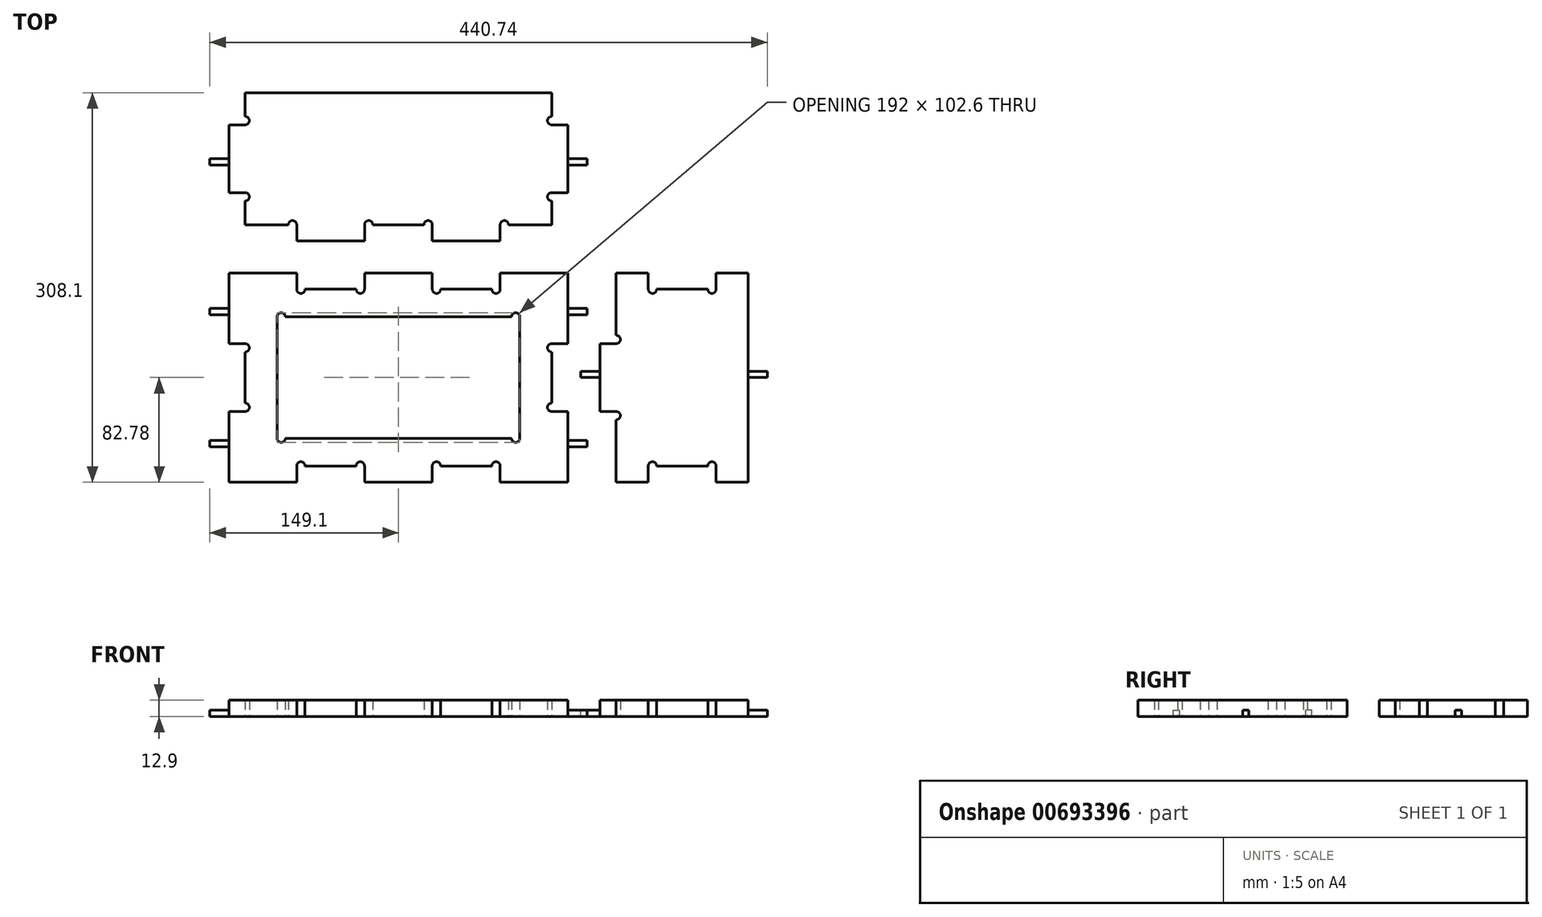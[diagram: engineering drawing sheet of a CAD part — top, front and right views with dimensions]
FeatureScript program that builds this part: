
annotation { "Feature Type Name" : "Feature", "Feature Type Description" : "" }
export const myFeature = defineFeature(function(context is Context, id is Id, definition is map)
    precondition{}
    {
        {
            assignVariable(context, id + "F0", {"name" : "thick", "anyValue" : 12.9 * mm});
        }
        {
            var Q0;
            Q0=qCreatedBy(makeId("Top.planeOp"),FACE);
            var sketch = newSketch(context, id + "F1", { "sketchPlane" : qUnion([Q0])});
            skLineSegment(sketch, "E0.bottom", {"start": v(96, -48) * mm, "end": v(-96, -48) * mm});
            skLineSegment(sketch, "E0.top", {"start": v(96, 48) * mm, "end": v(-96, 48) * mm});
            skLineSegment(sketch, "E0.left", {"start": v(96, -48) * mm, "end": v(96, 48) * mm});
            skLineSegment(sketch, "E0.right", {"start": v(-96, -48) * mm, "end": v(-96, 48) * mm});
            skPoint(sketch, "E0.middle", {"position": v(0, 0) * mm});
            skLineSegment(sketch, "E1", {"start": v(-134.1, 82.78) * mm, "end": v(-80.46, 82.78) * mm});
            skLineSegment(sketch, "E2", {"start": v(134.1, 82.78) * mm, "end": v(134.1, -82.78) * mm});
            skLineSegment(sketch, "E3", {"start": v(134.1, -82.78) * mm, "end": v(-134.1, -82.78) * mm});
            skLineSegment(sketch, "E4", {"start": v(-134.1, -82.78) * mm, "end": v(-134.1, 82.78) * mm});
            skPoint(sketch, "E5", {"position": v(0, 82.78) * mm});
            skPoint(sketch, "E6", {"position": v(134.1, 0) * mm});
            skLineSegment(sketch, "E7", {"start": v(-134.1, -82.78) * mm, "end": v(134.1, 82.78) * mm, "construction": true});
            skCircle(sketch, "E8", {"center": v(-92.7, 48) * mm, "radius": 3.3 * mm});
            skCircle(sketch, "E9", {"center": v(-92.7, -48) * mm, "radius": 3.3 * mm});
            skCircle(sketch, "E10", {"center": v(92.7, -48) * mm, "radius": 3.3 * mm});
            skCircle(sketch, "E11", {"center": v(92.7, 48) * mm, "radius": 3.3 * mm});
            skLineSegment(sketch, "E12", {"start": v(-80.46, 69.88) * mm, "end": v(-26.82, 69.88) * mm});
            skLineSegment(sketch, "E13", {"start": v(26.82, 69.88) * mm, "end": v(80.46, 69.88) * mm});
            skLineSegment(sketch, "E14", {"start": v(-80.46, 69.88) * mm, "end": v(-80.46, 82.78) * mm});
            skLineSegment(sketch, "E15", {"start": v(-26.82, 69.88) * mm, "end": v(-26.82, 82.78) * mm});
            skLineSegment(sketch, "E16", {"start": v(26.82, 69.88) * mm, "end": v(26.82, 82.78) * mm});
            skLineSegment(sketch, "E17", {"start": v(80.46, 69.88) * mm, "end": v(80.46, 82.78) * mm});
            skLineSegment(sketch, "E18", {"start": v(-80.46, 82.78) * mm, "end": v(-26.82, 82.78) * mm});
            skLineSegment(sketch, "E19", {"start": v(-26.82, 82.78) * mm, "end": v(26.82, 82.78) * mm});
            skLineSegment(sketch, "E20", {"start": v(26.82, 82.78) * mm, "end": v(80.46, 82.78) * mm});
            skLineSegment(sketch, "E21", {"start": v(80.46, 82.78) * mm, "end": v(134.1, 82.78) * mm});
            skLineSegment(sketch, "E22", {"start": v(-80.46, -82.78) * mm, "end": v(-80.46, -69.88) * mm});
            skLineSegment(sketch, "E23", {"start": v(-80.46, -69.88) * mm, "end": v(-26.82, -69.88) * mm});
            skLineSegment(sketch, "E24", {"start": v(-26.82, -69.88) * mm, "end": v(-26.82, -82.78) * mm});
            skLineSegment(sketch, "E25", {"start": v(26.82, -82.78) * mm, "end": v(26.82, -69.88) * mm});
            skLineSegment(sketch, "E26", {"start": v(26.82, -69.88) * mm, "end": v(80.46, -69.88) * mm});
            skLineSegment(sketch, "E27", {"start": v(80.46, -69.88) * mm, "end": v(80.46, -82.78) * mm});
            skLineSegment(sketch, "E28", {"start": v(134.1, 26.82) * mm, "end": v(121.2, 26.82) * mm});
            skLineSegment(sketch, "E29", {"start": v(121.2, 26.82) * mm, "end": v(121.2, -26.82) * mm});
            skLineSegment(sketch, "E30", {"start": v(121.2, -26.82) * mm, "end": v(134.1, -26.82) * mm});
            skPoint(sketch, "E31", {"position": v(121.2, 0) * mm});
            skLineSegment(sketch, "E32", {"start": v(-134.1, 26.82) * mm, "end": v(-121.2, 26.82) * mm});
            skLineSegment(sketch, "E33", {"start": v(-121.2, 26.82) * mm, "end": v(-121.2, -26.82) * mm});
            skLineSegment(sketch, "E34", {"start": v(-121.2, -26.82) * mm, "end": v(-134.1, -26.82) * mm});
            skCircle(sketch, "E35", {"center": v(-77.16, 69.88) * mm, "radius": 3.3 * mm});
            skCircle(sketch, "E36", {"center": v(-30.12, 69.88) * mm, "radius": 3.3 * mm});
            skCircle(sketch, "E37", {"center": v(30.12, 69.88) * mm, "radius": 3.3 * mm});
            skCircle(sketch, "E38", {"center": v(77.16, 69.88) * mm, "radius": 3.3 * mm});
            skCircle(sketch, "E39", {"center": v(121.2, 23.52) * mm, "radius": 3.3 * mm});
            skCircle(sketch, "E40", {"center": v(121.2, -23.52) * mm, "radius": 3.3 * mm});
            skCircle(sketch, "E41", {"center": v(77.16, -69.88) * mm, "radius": 3.3 * mm});
            skCircle(sketch, "E42", {"center": v(30.12, -69.88) * mm, "radius": 3.3 * mm});
            skCircle(sketch, "E43", {"center": v(-30.12, -69.88) * mm, "radius": 3.3 * mm});
            skCircle(sketch, "E44", {"center": v(-77.16, -69.88) * mm, "radius": 3.3 * mm});
            skCircle(sketch, "E45", {"center": v(-121.2, -23.52) * mm, "radius": 3.3 * mm});
            skCircle(sketch, "E46", {"center": v(-121.2, 23.52) * mm, "radius": 3.3 * mm});
            skLineSegment(sketch, "E47", {"start": v(-121.2, 120.88) * mm, "end": v(121.2, 120.88) * mm});
            skLineSegment(sketch, "E48", {"start": v(121.2, 120.88) * mm, "end": v(121.2, 225.32) * mm});
            skLineSegment(sketch, "E49", {"start": v(121.2, 225.32) * mm, "end": v(-121.2, 225.32) * mm});
            skLineSegment(sketch, "E50", {"start": v(-121.2, 225.32) * mm, "end": v(-121.2, 120.88) * mm});
            skLineSegment(sketch, "E51", {"start": v(-80.46, 120.88) * mm, "end": v(-80.46, 107.98) * mm});
            skLineSegment(sketch, "E52", {"start": v(-80.46, 107.98) * mm, "end": v(-26.82, 107.98) * mm});
            skLineSegment(sketch, "E53", {"start": v(-26.82, 107.98) * mm, "end": v(-26.82, 120.88) * mm});
            skLineSegment(sketch, "E54", {"start": v(26.82, 120.88) * mm, "end": v(26.82, 107.98) * mm});
            skLineSegment(sketch, "E55", {"start": v(26.82, 107.98) * mm, "end": v(80.46, 107.98) * mm});
            skLineSegment(sketch, "E56", {"start": v(80.46, 107.98) * mm, "end": v(80.46, 120.88) * mm});
            skCircle(sketch, "E57", {"center": v(23.52, 120.88) * mm, "radius": 3.3 * mm});
            skCircle(sketch, "E58", {"center": v(-23.52, 120.88) * mm, "radius": 3.3 * mm});
            skCircle(sketch, "E59", {"center": v(-83.76, 120.88) * mm, "radius": 3.3 * mm});
            skCircle(sketch, "E60", {"center": v(83.76, 120.88) * mm, "radius": 3.3 * mm});
            skLineSegment(sketch, "E61", {"start": v(134.1, 199.92) * mm, "end": v(134.1, 146.28) * mm});
            skPoint(sketch, "E62", {"position": v(121.2, 173.1) * mm});
            skPoint(sketch, "E63", {"position": v(134.1, 173.1) * mm});
            skLineSegment(sketch, "E64", {"start": v(134.1, 199.92) * mm, "end": v(121.2, 199.92) * mm});
            skLineSegment(sketch, "E65", {"start": v(134.1, 146.28) * mm, "end": v(121.2, 146.28) * mm});
            skCircle(sketch, "E66", {"center": v(121.2, 142.98) * mm, "radius": 3.3 * mm});
            skCircle(sketch, "E67", {"center": v(121.2, 203.22) * mm, "radius": 3.3 * mm});
            skLineSegment(sketch, "E68", {"start": v(-121.2, 146.28) * mm, "end": v(-134.1, 146.28) * mm});
            skLineSegment(sketch, "E69", {"start": v(-134.1, 146.28) * mm, "end": v(-134.1, 199.92) * mm});
            skLineSegment(sketch, "E70", {"start": v(-134.1, 199.92) * mm, "end": v(-121.2, 199.92) * mm});
            skCircle(sketch, "E71", {"center": v(-121.2, 203.22) * mm, "radius": 3.3 * mm});
            skCircle(sketch, "E72", {"center": v(-121.2, 142.98) * mm, "radius": 3.3 * mm});
            skLineSegment(sketch, "E73", {"start": v(172.2, 82.78) * mm, "end": v(172.2, -82.78) * mm});
            skLineSegment(sketch, "E74", {"start": v(276.64, -82.78) * mm, "end": v(276.64, 82.78) * mm});
            skLineSegment(sketch, "E75", {"start": v(276.64, 82.78) * mm, "end": v(172.2, 82.78) * mm});
            skLineSegment(sketch, "E76", {"start": v(172.2, 26.82) * mm, "end": v(159.3, 26.82) * mm});
            skLineSegment(sketch, "E77", {"start": v(159.3, 26.82) * mm, "end": v(159.3, -26.82) * mm});
            skLineSegment(sketch, "E78", {"start": v(159.3, -26.82) * mm, "end": v(172.2, -26.82) * mm});
            skLineSegment(sketch, "E79", {"start": v(172.2, -82.78) * mm, "end": v(276.64, -82.78) * mm});
            skLineSegment(sketch, "E80", {"start": v(197.6, 82.78) * mm, "end": v(197.6, 69.88) * mm});
            skLineSegment(sketch, "E81", {"start": v(197.6, 69.88) * mm, "end": v(251.24, 69.88) * mm});
            skLineSegment(sketch, "E82", {"start": v(251.24, 69.88) * mm, "end": v(251.24, 82.78) * mm});
            skLineSegment(sketch, "E83", {"start": v(197.6, -82.78) * mm, "end": v(197.6, -69.88) * mm});
            skLineSegment(sketch, "E84", {"start": v(197.6, -69.88) * mm, "end": v(251.24, -69.88) * mm});
            skLineSegment(sketch, "E85", {"start": v(251.24, -69.88) * mm, "end": v(251.24, -82.78) * mm});
            skPoint(sketch, "E86", {"position": v(224.42, 69.88) * mm});
            skPoint(sketch, "E87", {"position": v(224.42, 82.78) * mm});
            skCircle(sketch, "E88", {"center": v(172.2, 30.12) * mm, "radius": 3.3 * mm});
            skCircle(sketch, "E89", {"center": v(172.2, -30.12) * mm, "radius": 3.3 * mm});
            skCircle(sketch, "E90", {"center": v(200.9, -69.88) * mm, "radius": 3.3 * mm});
            skCircle(sketch, "E91", {"center": v(247.94, -69.88) * mm, "radius": 3.3 * mm});
            skCircle(sketch, "E92", {"center": v(247.94, 69.88) * mm, "radius": 3.3 * mm});
            skCircle(sketch, "E93", {"center": v(200.9, 69.88) * mm, "radius": 3.3 * mm});
            skLineSegment(sketch, "E94", {"start": v(-121.2, 120.88) * mm, "end": v(-121.2, 82.78) * mm, "construction": true});
            skLineSegment(sketch, "E95", {"start": v(121.2, 120.88) * mm, "end": v(121.2, 82.78) * mm, "construction": true});
            skLineSegment(sketch, "E96", {"start": v(-121.2, 101.83) * mm, "end": v(121.2, 101.83) * mm, "construction": true});
            skSolve(sketch);
        }
        {
            var Q0;
            {var subQ48=sQuery(id+"F1.wireOp",EDGE,"E0.left");Q0=makeQuery(id+"F1.imprint","IMPRINT",FACE,{"disambiguationData":[TD([[makeQuery(id+"F1.imprint","IMPRINT",EDGE,{"derivedFrom":subQ48}),-1.0]])]});}
            extrude(context, id + "F2", {"entities" : qUnion([Q0]), "depth" : getVariable(context, 'thick'), "offsetDistance" : 25 * mm});
        }
        {
            var Q0;
            {var subQ0=sQuery(id+"F1.wireOp",EDGE,"E49");Q0=makeQuery(id+"F1.imprint","IMPRINT",FACE,{"disambiguationData":[TD([[makeQuery(id+"F1.imprint","IMPRINT",EDGE,{"derivedFrom":subQ0}),1.0]])]});}
            var Q1;
            {var subQ0=sQuery(id+"F1.wireOp",EDGE,"E68");Q1=makeQuery(id+"F1.imprint","IMPRINT",FACE,{"disambiguationData":[TD([[makeQuery(id+"F1.imprint","IMPRINT",EDGE,{"derivedFrom":subQ0}),-1.0]])]});}
            var Q2;
            {var subQ0=sQuery(id+"F1.wireOp",EDGE,"E51");Q2=makeQuery(id+"F1.imprint","IMPRINT",FACE,{"disambiguationData":[TD([[makeQuery(id+"F1.imprint","IMPRINT",EDGE,{"derivedFrom":subQ0}),1.0]])]});}
            var Q3;
            {var subQ0=sQuery(id+"F1.wireOp",EDGE,"E54");Q3=makeQuery(id+"F1.imprint","IMPRINT",FACE,{"disambiguationData":[TD([[makeQuery(id+"F1.imprint","IMPRINT",EDGE,{"derivedFrom":subQ0}),1.0]])]});}
            var Q4;
            Q4=makeQuery(id+"F1.imprint","IMPRINT",FACE,{"disambiguationData":[TD([[makeQuery(id+"F1.imprint","IMPRINT",EDGE,{"derivedFrom":sQuery(id+"F1.wireOp",EDGE,"E61")}),-1.0]])]});
            extrude(context, id + "F3", {"entities" : qUnion([Q0, Q1, Q2, Q3, Q4]), "depth" : getVariable(context, 'thick'), "offsetDistance" : 25 * mm});
        }
        {
            var Q0;
            {var subQ1=sQuery(id+"F1.wireOp",EDGE,"E74");Q0=makeQuery(id+"F1.imprint","IMPRINT",FACE,{"disambiguationData":[TD([[makeQuery(id+"F1.imprint","IMPRINT",EDGE,{"derivedFrom":subQ1}),1.0]])]});}
            var Q1;
            {var subQ0=sQuery(id+"F1.wireOp",EDGE,"E76");Q1=makeQuery(id+"F1.imprint","IMPRINT",FACE,{"disambiguationData":[TD([[makeQuery(id+"F1.imprint","IMPRINT",EDGE,{"derivedFrom":subQ0}),1.0]])]});}
            extrude(context, id + "F4", {"entities" : qUnion([Q0, Q1]), "depth" : getVariable(context, 'thick'), "offsetDistance" : 25 * mm});
        }
        {
            var Q0;
            {var subQ0=sQuery(id+"F1.wireOp",EDGE,"E4");Q0=makeQuery(id+"F2.opExtrude","SWEPT_FACE",FACE,{"disambiguationData":[OSD([subQ0]),TDD([makeQuery(id+"F1.imprint","IMPRINT",EDGE,{"disambiguationData":[TD([[makeQuery(id+"F1.imprint","INTERSECT",VERTEX,{"derivedFrom":[sQuery(id+"F1.wireOp",EDGE,"E1"),subQ0]}),1.0]])],"derivedFrom":subQ0})])]});}
            var sketch = newSketch(context, id + "F5", { "sketchPlane" : qUnion([Q0])});
            skLineSegment(sketch, "E97", {"start": v(-54.8, 5) * mm, "end": v(-49.8, 5) * mm});
            skLineSegment(sketch, "E98", {"start": v(-49.8, 5) * mm, "end": v(-49.8, 0) * mm});
            skLineSegment(sketch, "E99", {"start": v(-49.8, 0) * mm, "end": v(-54.8, 0) * mm});
            skLineSegment(sketch, "E100", {"start": v(-54.8, 0) * mm, "end": v(-54.8, 5) * mm});
            skSolve(sketch);
        }
        {
            var Q0;
            Q0=makeQuery(id+"F5.imprint","IMPRINT",FACE,{"disambiguationData":[TD([[makeQuery(id+"F5.imprint","IMPRINT",EDGE,{"derivedFrom":sQuery(id+"F5.wireOp",EDGE,"E97")}),-1.0]])]});
            extrude(context, id + "F6", {"entities" : qUnion([Q0]), "operationType" : NewBodyOperationType.ADD, "depth" : 15 * mm, "offsetDistance" : 25 * mm});
        }
        {
            var Q0;
            {var subQ0=sQuery(id+"F1.wireOp",EDGE,"E4");Q0=makeQuery(id+"F2.opExtrude","SWEPT_FACE",FACE,{"disambiguationData":[OSD([subQ0]),TDD([makeQuery(id+"F1.imprint","IMPRINT",EDGE,{"disambiguationData":[TD([[makeQuery(id+"F1.imprint","INTERSECT",VERTEX,{"derivedFrom":[sQuery(id+"F1.wireOp",EDGE,"E3"),subQ0]}),-1.0]])],"derivedFrom":subQ0})])]});}
            var sketch = newSketch(context, id + "F7", { "sketchPlane" : qUnion([Q0])});
            skLineSegment(sketch, "E101.bottom", {"start": v(54.8, 0) * mm, "end": v(49.8, 0) * mm});
            skLineSegment(sketch, "E101.top", {"start": v(54.8, 5) * mm, "end": v(49.8, 5) * mm});
            skLineSegment(sketch, "E101.left", {"start": v(54.8, 0) * mm, "end": v(54.8, 5) * mm});
            skLineSegment(sketch, "E101.right", {"start": v(49.8, 0) * mm, "end": v(49.8, 5) * mm});
            skSolve(sketch);
        }
        {
            var Q0;
            Q0=makeQuery(id+"F7.imprint","IMPRINT",FACE,{"disambiguationData":[TD([[makeQuery(id+"F7.imprint","IMPRINT",EDGE,{"derivedFrom":sQuery(id+"F7.wireOp",EDGE,"E101.bottom")}),-1.0]])]});
            extrude(context, id + "F8", {"entities" : qUnion([Q0]), "operationType" : NewBodyOperationType.ADD, "depth" : 15 * mm, "offsetDistance" : 25 * mm});
        }
        {
            var Q0;
            {var subQ0=sQuery(id+"F1.wireOp",EDGE,"E2");Q0=makeQuery(id+"F2.opExtrude","SWEPT_FACE",FACE,{"disambiguationData":[OSD([subQ0]),TDD([makeQuery(id+"F1.imprint","IMPRINT",EDGE,{"disambiguationData":[TD([[makeQuery(id+"F1.imprint","INTERSECT",VERTEX,{"derivedFrom":[subQ0,sQuery(id+"F1.wireOp",EDGE,"E3")]}),1.0]])],"derivedFrom":subQ0})])]});}
            var sketch = newSketch(context, id + "F9", { "sketchPlane" : qUnion([Q0])});
            skLineSegment(sketch, "E102.bottom", {"start": v(-54.8, 0) * mm, "end": v(-49.8, 0) * mm});
            skLineSegment(sketch, "E102.top", {"start": v(-54.8, 5) * mm, "end": v(-49.8, 5) * mm});
            skLineSegment(sketch, "E102.left", {"start": v(-54.8, 0) * mm, "end": v(-54.8, 5) * mm});
            skLineSegment(sketch, "E102.right", {"start": v(-49.8, 0) * mm, "end": v(-49.8, 5) * mm});
            skSolve(sketch);
        }
        {
            var Q0;
            Q0=makeQuery(id+"F9.imprint","IMPRINT",FACE,{"disambiguationData":[TD([[makeQuery(id+"F9.imprint","IMPRINT",EDGE,{"derivedFrom":sQuery(id+"F9.wireOp",EDGE,"E102.bottom")}),-1.0]])]});
            extrude(context, id + "F10", {"entities" : qUnion([Q0]), "operationType" : NewBodyOperationType.ADD, "depth" : 15 * mm, "offsetDistance" : 25 * mm});
        }
        {
            var Q0;
            {var subQ0=sQuery(id+"F1.wireOp",EDGE,"E2");Q0=makeQuery(id+"F2.opExtrude","SWEPT_FACE",FACE,{"disambiguationData":[OSD([subQ0]),TDD([makeQuery(id+"F1.imprint","IMPRINT",EDGE,{"disambiguationData":[TD([[makeQuery(id+"F1.imprint","INTERSECT",VERTEX,{"derivedFrom":[subQ0,sQuery(id+"F1.wireOp",EDGE,"E21")]}),-1.0]])],"derivedFrom":subQ0})])]});}
            var sketch = newSketch(context, id + "F11", { "sketchPlane" : qUnion([Q0])});
            skLineSegment(sketch, "E103.bottom", {"start": v(54.8, 0) * mm, "end": v(49.8, 0) * mm});
            skLineSegment(sketch, "E103.top", {"start": v(54.8, 5) * mm, "end": v(49.8, 5) * mm});
            skLineSegment(sketch, "E103.left", {"start": v(54.8, 0) * mm, "end": v(54.8, 5) * mm});
            skLineSegment(sketch, "E103.right", {"start": v(49.8, 0) * mm, "end": v(49.8, 5) * mm});
            skSolve(sketch);
        }
        {
            var Q0;
            Q0=qSketchRegion(id+"F11",true);
            extrude(context, id + "F12", {"entities" : qUnion([Q0]), "operationType" : NewBodyOperationType.ADD, "depth" : 15 * mm, "offsetDistance" : 25 * mm});
        }
        {
            var Q0;
            Q0=makeQuery(id+"F3.opExtrude","SWEPT_FACE",FACE,{"disambiguationData":[OSD([sQuery(id+"F1.wireOp",EDGE,"E69")])]});
            var sketch = newSketch(context, id + "F13", { "sketchPlane" : qUnion([Q0])});
            skLineSegment(sketch, "E104.bottom", {"start": v(-173.1, 0) * mm, "end": v(-168.1, 0) * mm});
            skLineSegment(sketch, "E104.top", {"start": v(-173.1, 5) * mm, "end": v(-168.1, 5) * mm});
            skLineSegment(sketch, "E104.left", {"start": v(-173.1, 0) * mm, "end": v(-173.1, 5) * mm});
            skLineSegment(sketch, "E104.right", {"start": v(-168.1, 0) * mm, "end": v(-168.1, 5) * mm});
            skSolve(sketch);
        }
        {
            var Q0;
            Q0=qSketchRegion(id+"F13",true);
            var Q1;
            Q1=makeQuery(id+"F13.imprint","IMPRINT",FACE,{"disambiguationData":[TD([[makeQuery(id+"F13.imprint","IMPRINT",EDGE,{"derivedFrom":sQuery(id+"F13.wireOp",EDGE,"E104.bottom")}),-1.0]])]});
            extrude(context, id + "F14", {"entities" : qUnion([Q0, Q1]), "operationType" : NewBodyOperationType.ADD, "depth" : 15 * mm, "offsetDistance" : 25 * mm});
        }
        {
            var Q0;
            Q0=makeQuery(id+"F3.opExtrude","SWEPT_FACE",FACE,{"disambiguationData":[OSD([sQuery(id+"F1.wireOp",EDGE,"E61")])]});
            var sketch = newSketch(context, id + "F15", { "sketchPlane" : qUnion([Q0])});
            skLineSegment(sketch, "E105.bottom", {"start": v(173.1, 0) * mm, "end": v(168.1, 0) * mm});
            skLineSegment(sketch, "E105.top", {"start": v(173.1, 5) * mm, "end": v(168.1, 5) * mm});
            skLineSegment(sketch, "E105.left", {"start": v(173.1, 0) * mm, "end": v(173.1, 5) * mm});
            skLineSegment(sketch, "E105.right", {"start": v(168.1, 0) * mm, "end": v(168.1, 5) * mm});
            skSolve(sketch);
        }
        {
            var Q0;
            Q0=qSketchRegion(id+"F15",true);
            extrude(context, id + "F16", {"entities" : qUnion([Q0]), "operationType" : NewBodyOperationType.ADD, "depth" : 15 * mm, "offsetDistance" : 25 * mm});
        }
        {
            var Q0;
            Q0=makeQuery(id+"F4.opExtrude","SWEPT_FACE",FACE,{"disambiguationData":[OSD([sQuery(id+"F1.wireOp",EDGE,"E77")])]});
            var sketch = newSketch(context, id + "F17", { "sketchPlane" : qUnion([Q0])});
            skLineSegment(sketch, "E106.bottom", {"start": v(0, 0) * mm, "end": v(-5, 0) * mm});
            skLineSegment(sketch, "E106.top", {"start": v(0, 5) * mm, "end": v(-5, 5) * mm});
            skLineSegment(sketch, "E106.left", {"start": v(0, 0) * mm, "end": v(0, 5) * mm});
            skLineSegment(sketch, "E106.right", {"start": v(-5, 0) * mm, "end": v(-5, 5) * mm});
            skSolve(sketch);
        }
        {
            var Q0;
            Q0=makeQuery(id+"F17.imprint","IMPRINT",FACE,{"disambiguationData":[TD([[makeQuery(id+"F17.imprint","IMPRINT",EDGE,{"derivedFrom":sQuery(id+"F17.wireOp",EDGE,"E106.bottom")}),1.0]])]});
            extrude(context, id + "F18", {"entities" : qUnion([Q0]), "operationType" : NewBodyOperationType.ADD, "depth" : 15 * mm, "offsetDistance" : 25 * mm});
        }
        {
            var Q0;
            Q0=makeQuery(id+"F4.opExtrude","SWEPT_FACE",FACE,{"disambiguationData":[OSD([sQuery(id+"F1.wireOp",EDGE,"E74")])]});
            var sketch = newSketch(context, id + "F19", { "sketchPlane" : qUnion([Q0])});
            skLineSegment(sketch, "E107.bottom", {"start": v(0, 0) * mm, "end": v(5, 0) * mm});
            skLineSegment(sketch, "E107.top", {"start": v(0, 5) * mm, "end": v(5, 5) * mm});
            skLineSegment(sketch, "E107.left", {"start": v(0, 0) * mm, "end": v(0, 5) * mm});
            skLineSegment(sketch, "E107.right", {"start": v(5, 0) * mm, "end": v(5, 5) * mm});
            skSolve(sketch);
        }
        {
            var Q0;
            Q0=makeQuery(id+"F19.imprint","IMPRINT",FACE,{"disambiguationData":[TD([[makeQuery(id+"F19.imprint","IMPRINT",EDGE,{"derivedFrom":sQuery(id+"F19.wireOp",EDGE,"E107.bottom")}),1.0]])]});
            extrude(context, id + "F20", {"entities" : qUnion([Q0]), "operationType" : NewBodyOperationType.ADD, "depth" : 15 * mm, "offsetDistance" : 25 * mm});
        }
    });
